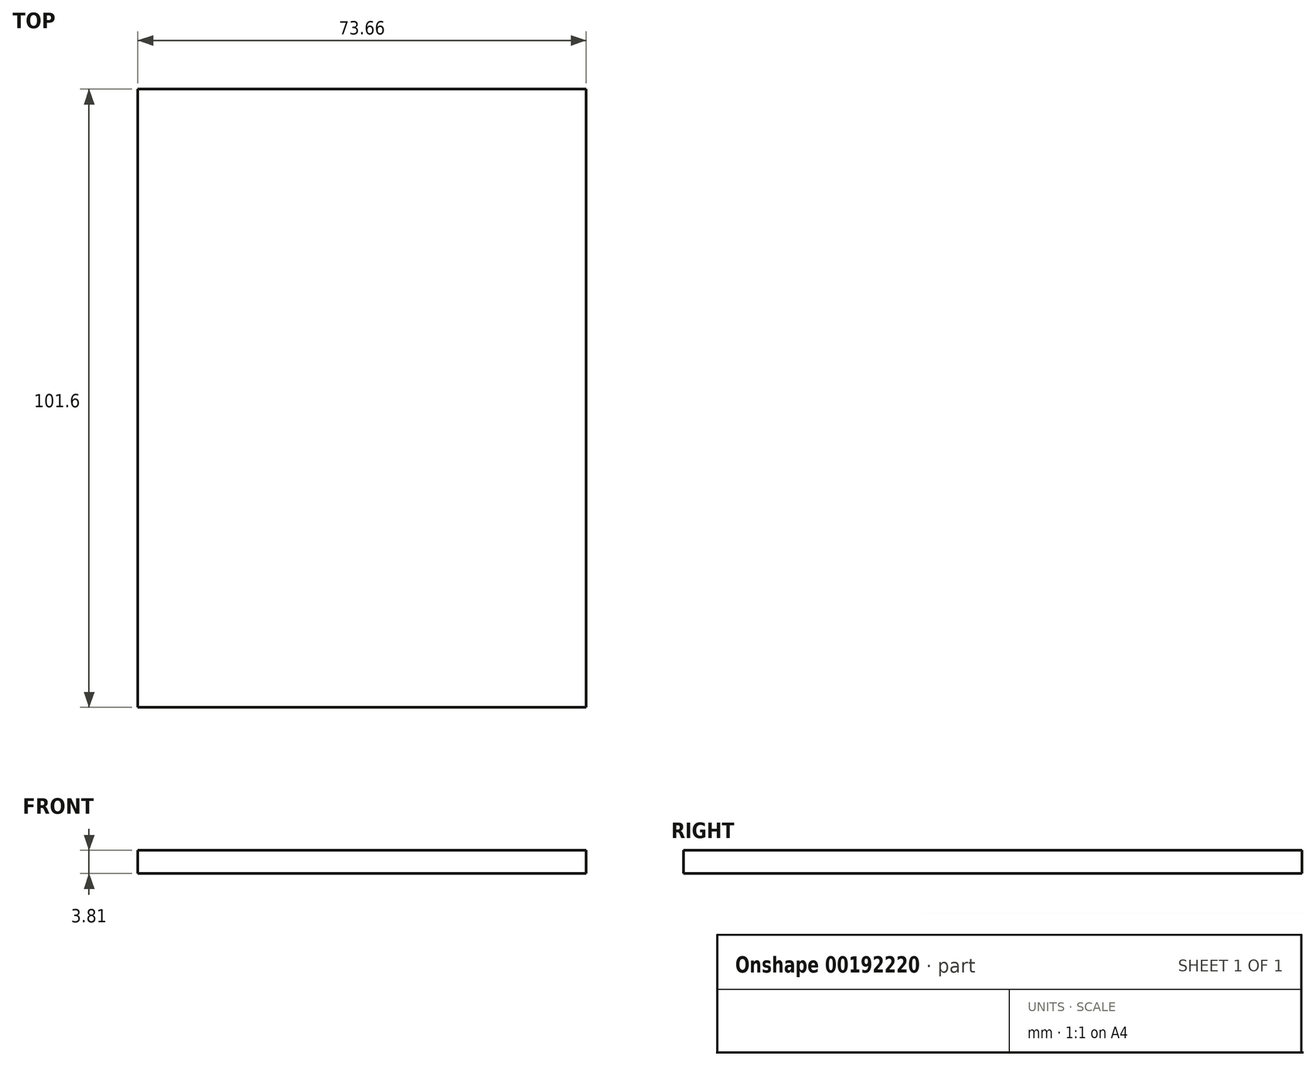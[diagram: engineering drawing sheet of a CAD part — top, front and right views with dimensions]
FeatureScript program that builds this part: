
annotation { "Feature Type Name" : "Feature", "Feature Type Description" : "" }
export const myFeature = defineFeature(function(context is Context, id is Id, definition is map)
    precondition{}
    {
        {
            var Q0;
            Q0=qCreatedBy(makeId("Top.planeOp"),FACE);
            var sketch = newSketch(context, id + "F0", { "sketchPlane" : qUnion([Q0])});
            skLineSegment(sketch, "E0.bottom", {"start": v(36.83, 50.8) * mm, "end": v(-36.83, 50.8) * mm});
            skLineSegment(sketch, "E0.top", {"start": v(36.83, -50.8) * mm, "end": v(-36.83, -50.8) * mm});
            skLineSegment(sketch, "E0.left", {"start": v(36.83, 50.8) * mm, "end": v(36.83, -50.8) * mm});
            skLineSegment(sketch, "E0.right", {"start": v(-36.83, 50.8) * mm, "end": v(-36.83, -50.8) * mm});
            skPoint(sketch, "E0.middle", {"position": v(0, 0) * mm});
            skSolve(sketch);
        }
        {
            var Q0;
            Q0=makeQuery(id+"F0.imprint","IMPRINT",FACE,{"disambiguationData":[TD([[makeQuery(id+"F0.imprint","IMPRINT",EDGE,{"derivedFrom":sQuery(id+"F0.wireOp",EDGE,"E0.bottom")}),1.0]])]});
            extrude(context, id + "F1", {"entities" : qUnion([Q0]), "depth" : 3.8 * mm});
        }
    });
